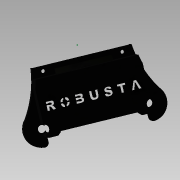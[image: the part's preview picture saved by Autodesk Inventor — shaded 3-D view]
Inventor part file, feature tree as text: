
AUTODESK INVENTOR PART (.ipt)
format: ipt  version: 2015 SP1 (Build 190203100, 203)  size: 800,768 bytes
history: native  units: mm
features: sketch x18, extrude x16, projected_geometry x8, fillet x5, plane x4
ambient origin geometry x8: Origin, YZ Plane, XZ Plane, XY Plane, X Axis, Y Axis, Z Axis, Center Point
bodies: Body1 (feature_tree), Body2 (feature_tree)
feature tree (51):
  plane  "Work Plane2"
  sketch  "Sketch12"  dims[d19=46.65mm d72=0.0mm d125=-8.5mm d129=3.5mm]
  plane  "Work Plane3"
  extrude  "Extrusion9"  Depth=3.5mm
  extrude  "Extrusion10"  Depth=7.0mm TaperAngle=0.0deg
  extrude  "Extrusion11"  Depth=13.5mm TaperAngle=0.0deg
  extrude  "Extrusion12"  Depth=3.5mm TaperAngle=0.0deg
  extrude  "Extrusion13"  Depth=3.5mm TaperAngle=0.0deg
  extrude  "Extrusion14"  Depth=4.46mm
  extrude  "Extrusion15"  Depth=50.0mm TaperAngle=0.0deg
  plane  "Work Plane4"
  extrude  "Extrusion16"  Depth=7.1mm
  extrude  "Extrusion17"  Depth=7.1mm
  extrude  "Extrusion18"  Depth=7.1mm
  extrude  "Extrusion19"  Depth=8.0mm
  extrude  "Extrusion20"  TaperAngle=90.0deg  [1 undecoded]
  extrude  "Extrusion21"  Depth=80.0mm TaperAngle=0.0deg
  fillet  "Fillet1"  Radius=13.5mm
  extrude  "Extrusion22"  Depth=13.5mm TaperAngle=0.0deg
  fillet  "Fillet2"  Radius=4.0mm
  fillet  "Fillet3"  Radius=4.0mm
  fillet  "Fillet4"  Radius=4.0mm
  extrude  "Extrusion23"  Depth=1.0mm
  fillet  "Fillet5"  [1 undecoded]
  extrude  "Extrusion24"  Depth=2.0mm
  sketch  "Sketch34"  dims[d202=46.987914mm]
  sketch  "Sketch35"  dims[d203=12.02274mm d204=3.5mm d205=3.5mm d206=0.0mm d207=-42.0mm]
  plane  "Work Plane5"
  sketch  "Sketch13"  dims[d136=-5.0mm d137=7.0mm d138=0.0mm]
  sketch  "Sketch14"  dims[d139=3.5mm d140=0.0mm d143=13.5mm d144=0.0mm]
  sketch  "Sketch16"  dims[d145=3.5mm d146=0.0mm d147=3.5mm d148=0.0mm]
  projected_geometry  "Projected Loop1"
  projected_geometry  "Projected Loop2"
  projected_geometry  "Projected Loop3"
  sketch  "Sketch17"  dims[d149=3.5mm d150=0.0mm d158=3.5mm d159=0.0mm]
  sketch  "Sketch18"  dims[d161=0.0mm d162=4.46mm]
  projected_geometry  "Projected Loop4"
  sketch  "Sketch19"  dims[d163=45.0deg d164=50.0mm d165=0.0mm]
  projected_geometry  "Projected Loop6"
  sketch  "Sketch20"  dims[d166=7.1mm d167=7.1mm]
  sketch  "Sketch21"  dims[d168=0.0mm d169=0.0mm d170=7.1mm]
  sketch  "Sketch22"  dims[d171=50.0mm d172=0.0mm d173=7.1mm]
  sketch  "Sketch25"  dims[d174=50.0mm d175=0.0mm d178=8.0mm]
  sketch  "Sketch29"  dims[d180=11.0mm d182=90.0deg]
  sketch  "Sketch30"  dims[d183=0.5mm d186=80.0mm d187=0.0mm d188=13.5mm d189=0.0mm]
  projected_geometry  "Projected Loop14"
  sketch  "Sketch31"  dims[d190=4.0mm d191=13.5mm d192=0.0mm d193=4.0mm d194=4.0mm d195=4.0mm]
  sketch  "Sketch32"  dims[d196=1.0mm d197=1.0mm d198=0.0mm]
  projected_geometry  "Projected Loop15"
  projected_geometry  "Projected Loop16"
  sketch  "Sketch33"  dims[d199=3.5mm d200=0.0mm d201=2.0mm]
note: 2 required parameter values undecoded (feature->parameter linkage not recoverable at this tier; creation-order binding heuristic only, values carry confidence <= 0.55)
